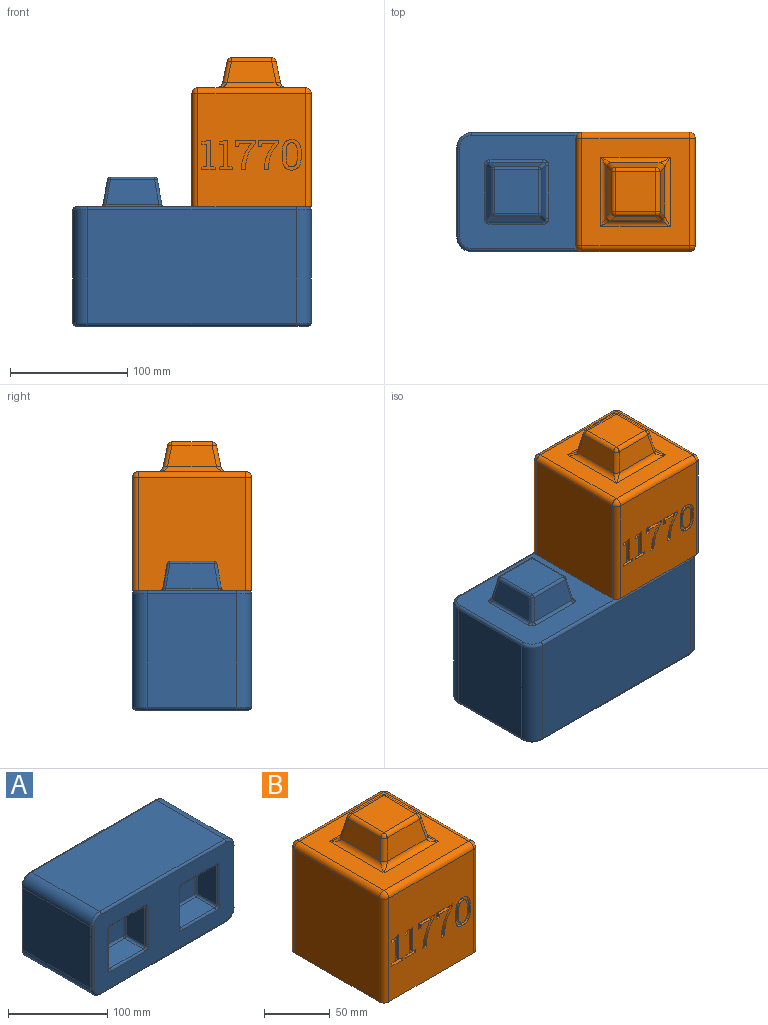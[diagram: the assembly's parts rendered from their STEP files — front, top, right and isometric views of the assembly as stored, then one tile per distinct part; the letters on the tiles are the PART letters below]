
ASSEMBLY  parts=2 mates=1
PART A: 196 faces, bbox 205.4x127.2x103.8 mm
  f0: bspline ~3.55x3.2mm, area 9.5mm2, adj f8,f130,f132,f133
  f1: bspline ~3.55x3.2mm, area 9.5mm2, adj f8,f82,f129,f131
  f2: bspline ~3.55x3.2mm, area 9.5mm2, adj f8,f122,f124,f125
  f3: bspline ~3.55x3.2mm, area 9.5mm2, adj f8,f70,f121,f123
  f4: bspline ~3.55x3.2mm, area 9.5mm2, adj f8,f84,f87,f88
  f5: bspline ~3.55x3.2mm, area 9.5mm2, adj f8,f82,f83,f86
  f6: bspline ~3.55x3.2mm, area 9.5mm2, adj f8,f72,f75,f76
  f7: bspline ~3.55x3.2mm, area 9.5mm2, adj f8,f70,f71,f74
  f8: plane 198.14x96.54mm, normal (0,1,0), area 13012.7mm2, adj f0,f1,f2,f3,f4,f5,f6,f7
  f9: plane 96.52x76.2mm, normal (1,0,0), area 7354.8mm2, adj f29,f31,f40,f94
  f10: plane 177.8x96.52mm, normal (0,0,-1), area 17161.3mm2, adj f29,f30,f33,f37
  f11: plane 96.52x76.2mm, normal (-1,0,0), area 7354.8mm2, adj f30,f34,f38,f95
  f12: plane 198.27x96.67mm, normal (0,-1,0), area 12440.4mm2, adj f36,f37,f38,f39,f40,f46,f47,f49
  f13: plane 45.06x21.2mm, normal (0.98,0.17,0), area 889.6mm2, adj f77,f82,f83,f129
  f14: plane 45.06x21.2mm, normal (0,0.17,-0.98), area 889.6mm2, adj f78,f83,f84,f88
  f15: plane 45.06x21.2mm, normal (-0.98,0.17,0), area 889.6mm2, adj f79,f84,f85,f130
  f16: plane 37.58x37.58mm, normal (0,1,0), area 1412.3mm2, adj f77,f78,f79,f126
  f17: plane 45.06x21.2mm, normal (0.98,0.17,0), area 889.6mm2, adj f65,f70,f71,f121
  f18: plane 45.06x21.2mm, normal (0,0.17,-0.98), area 889.6mm2, adj f66,f71,f72,f76
  f19: plane 45.06x21.2mm, normal (-0.98,0.17,0), area 889.6mm2, adj f67,f72,f73,f122
  f20: plane 37.58x37.58mm, normal (0,1,0), area 1412.3mm2, adj f65,f66,f67,f118
  f21: plane 47.6x22.47mm, normal (-0.98,-0.17,0), area 995.7mm2, adj f45,f50,f52,f108
  f22: plane 47.6x22.47mm, normal (0,-0.17,0.98), area 995.7mm2, adj f43,f44,f49,f50
  f23: plane 47.6x22.47mm, normal (0.98,-0.17,0), area 995.7mm2, adj f41,f43,f46,f103
  f24: plane 39.67x39.67mm, normal (0,-1,0), area 1573.9mm2, adj f41,f44,f45,f104
  f25: plane 47.6x22.47mm, normal (-0.98,-0.17,0), area 995.7mm2, adj f55,f60,f61,f114
  f26: plane 47.6x22.47mm, normal (0,-0.17,0.98), area 995.7mm2, adj f54,f59,f60,f64
  f27: plane 47.6x22.47mm, normal (0.98,-0.17,0), area 995.7mm2, adj f53,f58,f59,f113
  f28: plane 39.67x39.67mm, normal (0,-1,0), area 1573.9mm2, adj f53,f54,f55,f110
  f29: cylinder r=12.7mm len=96.52mm, axis (0,-1,0), area 1925.5mm2, adj f9,f10,f32,f39
  f30: cylinder r=12.7mm len=96.52mm, axis (0,-1,0), area 1925.5mm2, adj f10,f11,f35,f36
  f31: cylinder r=2.54mm len=76.2mm, axis (0,0,-1), area 304mm2, adj f8,f9,f32,f96
  f32: torus R=10.16mm, axis (0,-1,0), area 73.8mm2, adj f8,f29,f31,f33
  f33: cylinder r=2.54mm len=177.8mm, axis (-1,0,0), area 709.4mm2, adj f8,f10,f32,f35
  f34: cylinder r=2.54mm len=76.2mm, axis (0,0,1), area 304mm2, adj f8,f11,f35,f98
  f35: torus R=10.16mm, axis (0,-1,0), area 73.8mm2, adj f8,f30,f33,f34
  f36: torus R=10.16mm, axis (0,-1,0), area 73.8mm2, adj f12,f30,f37,f38
  f37: cylinder r=2.54mm len=177.8mm, axis (1,0,0), area 709.4mm2, adj f10,f12,f36,f39
  f38: cylinder r=2.54mm len=76.2mm, axis (0,0,-1), area 304mm2, adj f11,f12,f36,f99
  f39: torus R=10.16mm, axis (0,-1,0), area 73.8mm2, adj f12,f29,f37,f40
  f40: cylinder r=2.54mm len=76.2mm, axis (0,0,1), area 304mm2, adj f9,f12,f39,f101
  f41: cylinder r=2.54mm len=39.67mm, axis (0,0,-1), area 140.7mm2, adj f23,f24,f42,f102
  f42: sphere r=2.54mm, area 8.4mm2, adj f41,f43,f44
  f43: cylinder r=2.54mm len=22.99mm, axis (0.17,0.97,0.17), area 91.6mm2, adj f22,f23,f42,f47
  f44: cylinder r=2.54mm len=39.67mm, axis (1,0,0), area 140.7mm2, adj f22,f24,f42,f48
  f45: cylinder r=2.54mm len=39.67mm, axis (0,0,1), area 140.7mm2, adj f21,f24,f48,f106
  f46: cylinder r=2.54mm len=47.6mm, axis (0,0,1), area 168.8mm2, adj f12,f23,f47,f105
  f47: bspline ~5x5mm, area 19.1mm2, adj f12,f43,f46,f49
  f48: sphere r=2.54mm, area 7.9mm2, adj f44,f45,f50
  f49: cylinder r=2.54mm len=47.6mm, axis (-1,0,0), area 168.8mm2, adj f12,f22,f47,f51
  f50: cylinder r=2.54mm len=22.99mm, axis (-0.17,0.97,0.17), area 91.6mm2, adj f21,f22,f48,f51
  f51: bspline ~5x5mm, area 19.1mm2, adj f12,f49,f50,f52
  f52: cylinder r=2.54mm len=47.6mm, axis (0,0,-1), area 168.8mm2, adj f12,f21,f51,f109
  f53: cylinder r=2.54mm len=39.67mm, axis (0,0,-1), area 140.7mm2, adj f27,f28,f56,f111
  f54: cylinder r=2.54mm len=39.67mm, axis (1,0,0), area 140.7mm2, adj f26,f28,f56,f57
  f55: cylinder r=2.54mm len=39.67mm, axis (0,0,1), area 140.7mm2, adj f25,f28,f57,f112
  f56: sphere r=2.54mm, area 8.4mm2, adj f53,f54,f59
  f57: sphere r=2.54mm, area 7.9mm2, adj f54,f55,f60
  f58: cylinder r=2.54mm len=47.6mm, axis (0,0,1), area 168.8mm2, adj f12,f27,f62,f115
  f59: cylinder r=2.54mm len=22.99mm, axis (0.17,0.97,0.17), area 91.6mm2, adj f26,f27,f56,f62
  f60: cylinder r=2.54mm len=22.99mm, axis (-0.17,0.97,0.17), area 91.6mm2, adj f25,f26,f57,f63
  f61: cylinder r=2.54mm len=47.6mm, axis (0,0,-1), area 168.8mm2, adj f12,f25,f63,f116
  f62: bspline ~5x5mm, area 19.1mm2, adj f12,f58,f59,f64
  f63: bspline ~5x5mm, area 19.1mm2, adj f12,f60,f61,f64
  f64: cylinder r=2.54mm len=47.6mm, axis (-1,0,0), area 168.8mm2, adj f12,f26,f62,f63
  f65: cylinder r=2.54mm len=37.58mm, axis (0,0,1), area 133.3mm2, adj f17,f20,f68,f119
  f66: cylinder r=2.54mm len=37.58mm, axis (1,0,0), area 133.3mm2, adj f18,f20,f68,f69
  f67: cylinder r=2.54mm len=37.58mm, axis (0,0,-1), area 133.3mm2, adj f19,f20,f69,f120
  f68: sphere r=2.54mm, area 7.9mm2, adj f65,f66,f71
  f69: sphere r=2.54mm, area 8.4mm2, adj f66,f67,f72
  f70: cylinder r=2.54mm len=45.06mm, axis (0,0,-1), area 159.8mm2, adj f3,f7,f8,f17
  f71: cylinder r=2.54mm len=21.72mm, axis (0.17,-0.97,-0.17), area 86.2mm2, adj f7,f17,f18,f68,f74
  f72: cylinder r=2.54mm len=21.72mm, axis (-0.17,-0.97,-0.17), area 86.2mm2, adj f6,f18,f19,f69,f75
  f73: cylinder r=2.54mm len=45.06mm, axis (0,0,1), area 159.8mm2, adj f8,f19,f75,f124
  f74: bspline ~3.55x3.2mm, area 9.5mm2, adj f7,f8,f71,f76
  f75: bspline ~3.55x3.2mm, area 9.5mm2, adj f6,f8,f72,f73
  f76: cylinder r=2.54mm len=45.06mm, axis (-1,0,0), area 159.8mm2, adj f6,f8,f18,f74
  f77: cylinder r=2.54mm len=37.58mm, axis (0,0,1), area 133.3mm2, adj f13,f16,f80,f127
  f78: cylinder r=2.54mm len=37.58mm, axis (1,0,0), area 133.3mm2, adj f14,f16,f80,f81
  f79: cylinder r=2.54mm len=37.58mm, axis (0,0,-1), area 133.3mm2, adj f15,f16,f81,f128
  f80: sphere r=2.54mm, area 7.9mm2, adj f77,f78,f83
  f81: sphere r=2.54mm, area 8.4mm2, adj f78,f79,f84
  f82: cylinder r=2.54mm len=45.06mm, axis (0,0,-1), area 159.8mm2, adj f1,f5,f8,f13
  f83: cylinder r=2.54mm len=21.72mm, axis (0.17,-0.97,-0.17), area 86.2mm2, adj f5,f13,f14,f80,f86
  f84: cylinder r=2.54mm len=21.72mm, axis (-0.17,-0.97,-0.17), area 86.2mm2, adj f4,f14,f15,f81,f87
  f85: cylinder r=2.54mm len=45.06mm, axis (0,0,1), area 159.8mm2, adj f8,f15,f87,f132
  f86: bspline ~3.55x3.2mm, area 9.5mm2, adj f5,f8,f83,f88
  f87: bspline ~3.55x3.2mm, area 9.5mm2, adj f4,f8,f84,f85
  f88: cylinder r=2.54mm len=45.06mm, axis (-1,0,0), area 159.8mm2, adj f4,f8,f14,f86
  f89: plane 177.8x96.52mm, normal (0,0,1), area 17161.3mm2, adj f94,f95,f97,f100
  f90: plane 45.06x21.2mm, normal (0,0.17,0.98), area 889.6mm2, adj f126,f129,f130,f133
  f91: plane 45.06x21.2mm, normal (0,0.17,0.98), area 889.6mm2, adj f118,f121,f122,f125
  f92: plane 47.6x22.47mm, normal (0,-0.17,-0.98), area 995.7mm2, adj f103,f104,f107,f108
  f93: plane 47.6x22.47mm, normal (0,-0.17,-0.98), area 995.7mm2, adj f110,f113,f114,f117
  f94: cylinder r=12.7mm len=96.52mm, axis (0,-1,0), area 1925.5mm2, adj f9,f89,f96,f101
  f95: cylinder r=12.7mm len=96.52mm, axis (0,-1,0), area 1925.5mm2, adj f11,f89,f98,f99
  f96: torus R=10.16mm, axis (0,-1,0), area 73.8mm2, adj f8,f31,f94,f97
  f97: cylinder r=2.54mm len=177.8mm, axis (-1,0,0), area 709.4mm2, adj f8,f89,f96,f98
  f98: torus R=10.16mm, axis (0,-1,0), area 73.8mm2, adj f8,f34,f95,f97
  f99: torus R=10.16mm, axis (0,-1,0), area 73.8mm2, adj f12,f38,f95,f100
  f100: cylinder r=2.54mm len=177.8mm, axis (1,0,0), area 709.4mm2, adj f12,f89,f99,f101
  f101: torus R=10.16mm, axis (0,-1,0), area 73.8mm2, adj f12,f40,f94,f100
  f102: sphere r=2.54mm, area 8.4mm2, adj f41,f103,f104
  f103: cylinder r=2.54mm len=22.99mm, axis (0.17,0.97,-0.17), area 91.6mm2, adj f23,f92,f102,f105
  f104: cylinder r=2.54mm len=39.67mm, axis (1,0,0), area 140.7mm2, adj f24,f92,f102,f106
  f105: bspline ~5x5mm, area 19.1mm2, adj f12,f46,f103,f107
  f106: sphere r=2.54mm, area 7.9mm2, adj f45,f104,f108
  f107: cylinder r=2.54mm len=47.6mm, axis (-1,0,0), area 168.8mm2, adj f12,f92,f105,f109
  f108: cylinder r=2.54mm len=22.99mm, axis (-0.17,0.97,-0.17), area 91.6mm2, adj f21,f92,f106,f109
  f109: bspline ~5x5mm, area 19.1mm2, adj f12,f52,f107,f108
  f110: cylinder r=2.54mm len=39.67mm, axis (1,0,0), area 140.7mm2, adj f28,f93,f111,f112
  f111: sphere r=2.54mm, area 8.4mm2, adj f53,f110,f113
  f112: sphere r=2.54mm, area 7.9mm2, adj f55,f110,f114
  f113: cylinder r=2.54mm len=22.99mm, axis (0.17,0.97,-0.17), area 91.6mm2, adj f27,f93,f111,f115
  f114: cylinder r=2.54mm len=22.99mm, axis (-0.17,0.97,-0.17), area 91.6mm2, adj f25,f93,f112,f116
  f115: bspline ~5x5mm, area 19.1mm2, adj f12,f58,f113,f117
  f116: bspline ~5x5mm, area 19.1mm2, adj f12,f61,f114,f117
  f117: cylinder r=2.54mm len=47.6mm, axis (-1,0,0), area 168.8mm2, adj f12,f93,f115,f116
  f118: cylinder r=2.54mm len=37.58mm, axis (1,0,0), area 133.3mm2, adj f20,f91,f119,f120
  f119: sphere r=2.54mm, area 7.9mm2, adj f65,f118,f121
  f120: sphere r=2.54mm, area 8.4mm2, adj f67,f118,f122
  f121: cylinder r=2.54mm len=21.72mm, axis (0.17,-0.97,0.17), area 86.2mm2, adj f3,f17,f91,f119,f123
  f122: cylinder r=2.54mm len=21.72mm, axis (-0.17,-0.97,0.17), area 86.2mm2, adj f2,f19,f91,f120,f124
  f123: bspline ~3.55x3.2mm, area 9.5mm2, adj f3,f8,f121,f125
  f124: bspline ~3.55x3.2mm, area 9.5mm2, adj f2,f8,f73,f122
  f125: cylinder r=2.54mm len=45.06mm, axis (-1,0,0), area 159.8mm2, adj f2,f8,f91,f123
  f126: cylinder r=2.54mm len=37.58mm, axis (1,0,0), area 133.3mm2, adj f16,f90,f127,f128
  f127: sphere r=2.54mm, area 7.9mm2, adj f77,f126,f129
  f128: sphere r=2.54mm, area 8.4mm2, adj f79,f126,f130
  f129: cylinder r=2.54mm len=21.72mm, axis (0.17,-0.97,0.17), area 86.2mm2, adj f1,f13,f90,f127,f131
  f130: cylinder r=2.54mm len=21.72mm, axis (-0.17,-0.97,0.17), area 86.2mm2, adj f0,f15,f90,f128,f132
  f131: bspline ~3.55x3.2mm, area 9.5mm2, adj f1,f8,f129,f133
  f132: bspline ~3.55x3.2mm, area 9.5mm2, adj f0,f8,f85,f130
  f133: cylinder r=2.54mm len=45.06mm, axis (-1,0,0), area 159.8mm2, adj f0,f8,f90,f131
  f134: sphere r=5.08mm, area 31.7mm2, adj f135,f145,f194
  f135: cylinder r=5.08mm len=39.67mm, axis (1,0,0), area 281.4mm2, adj f134,f136,f144,f193
  f136: sphere r=5.08mm, area 31.7mm2, adj f135,f143,f192
  f137: sphere r=5.08mm, area 31.7mm2, adj f138,f142,f189
  f138: cylinder r=5.08mm len=39.67mm, axis (1,0,0), area 281.4mm2, adj f137,f139,f141,f188
  f139: sphere r=5.08mm, area 31.7mm2, adj f138,f140,f187
  f140: cylinder r=5.08mm len=23.17mm, axis (0.17,0.97,-0.17), area 183.1mm2, adj f139,f141,f185,f186
  f141: plane 47.6x22.47mm, normal (0,0.17,0.98), area 995.7mm2, adj f138,f140,f142,f185
  f142: cylinder r=5.08mm len=23.17mm, axis (-0.17,0.97,-0.17), area 183.1mm2, adj f137,f141,f185,f190
  f143: cylinder r=5.08mm len=23.17mm, axis (0.17,0.97,-0.17), area 183.1mm2, adj f136,f144,f185,f191
  f144: plane 47.6x22.47mm, normal (0,0.17,0.98), area 995.7mm2, adj f135,f143,f145,f185
  f145: cylinder r=5.08mm len=23.17mm, axis (-0.17,0.97,-0.17), area 183.1mm2, adj f134,f144,f185,f195
  f146: plane 45.06x21.2mm, normal (0,-0.17,-0.98), area 889.6mm2, adj f151,f180,f181,f182
  f147: plane 45.06x21.2mm, normal (0,-0.17,-0.98), area 889.6mm2, adj f150,f175,f176,f177
  f148: cylinder r=10.16mm len=96.52mm, axis (0,-1,0), area 1540.4mm2, adj f149,f173,f184,f185
  f149: plane 177.8x96.52mm, normal (0,0,-1), area 17161.3mm2, adj f148,f152,f173,f185
  f150: cylinder r=5.08mm len=55.06mm, axis (-1,0,0), area 347.9mm2, adj f147,f173,f174,f178
  f151: cylinder r=5.08mm len=55.06mm, axis (-1,0,0), area 347.9mm2, adj f146,f173,f179,f183
  f152: cylinder r=10.16mm len=96.52mm, axis (0,-1,0), area 1540.4mm2, adj f149,f172,f173,f185
  f153: sphere r=5.08mm, area 31.7mm2, adj f154,f159,f194
  f154: cylinder r=5.08mm len=39.67mm, axis (1,0,0), area 281.4mm2, adj f153,f155,f160,f193
  f155: sphere r=5.08mm, area 31.7mm2, adj f154,f161,f192
  f156: sphere r=5.08mm, area 31.7mm2, adj f157,f162,f189
  f157: cylinder r=5.08mm len=39.67mm, axis (1,0,0), area 281.4mm2, adj f156,f158,f163,f188
  f158: sphere r=5.08mm, area 31.7mm2, adj f157,f164,f187
  f159: cylinder r=5.08mm len=23.17mm, axis (-0.17,0.97,0.17), area 183.1mm2, adj f153,f160,f185,f195
  f160: plane 47.6x22.47mm, normal (0,0.17,-0.98), area 995.7mm2, adj f154,f159,f161,f185
  f161: cylinder r=5.08mm len=23.17mm, axis (0.17,0.97,0.17), area 183.1mm2, adj f155,f160,f185,f191
  f162: cylinder r=5.08mm len=23.17mm, axis (-0.17,0.97,0.17), area 183.1mm2, adj f156,f163,f185,f190
  f163: plane 47.6x22.47mm, normal (0,0.17,-0.98), area 995.7mm2, adj f157,f162,f164,f185
  f164: cylinder r=5.08mm len=23.17mm, axis (0.17,0.97,0.17), area 183.1mm2, adj f158,f163,f185,f186
  f165: plane 45.06x21.2mm, normal (0,-0.17,0.98), area 889.6mm2, adj f167,f180,f181,f182
  f166: plane 45.06x21.2mm, normal (0,-0.17,0.98), area 889.6mm2, adj f168,f175,f176,f177
  f167: cylinder r=5.08mm len=55.06mm, axis (-1,0,0), area 347.9mm2, adj f165,f173,f179,f183
  f168: cylinder r=5.08mm len=55.06mm, axis (-1,0,0), area 347.9mm2, adj f166,f173,f174,f178
  f169: plane 177.8x96.52mm, normal (0,0,1), area 17161.3mm2, adj f170,f171,f173,f185
  f170: cylinder r=10.16mm len=96.52mm, axis (0,-1,0), area 1540.4mm2, adj f169,f173,f184,f185
  f171: cylinder r=10.16mm len=96.52mm, axis (0,-1,0), area 1540.4mm2, adj f169,f172,f173,f185
  f172: plane 96.52x76.2mm, normal (-1,0,0), area 7354.8mm2, adj f152,f171,f173,f185
  f173: plane 198.12x96.52mm, normal (0,-1,0), area 12970.1mm2, adj f148,f149,f150,f151,f152,f167,f168,f169
  f174: cylinder r=5.08mm len=55.06mm, axis (0,0,-1), area 347.9mm2, adj f150,f168,f173,f175
  f175: plane 45.06x21.2mm, normal (-0.98,-0.17,0), area 889.6mm2, adj f147,f166,f174,f176
  f176: plane 37.58x37.58mm, normal (0,-1,0), area 1412.3mm2, adj f147,f166,f175,f177
  f177: plane 45.06x21.2mm, normal (0.98,-0.17,0), area 889.6mm2, adj f147,f166,f176,f178
  f178: cylinder r=5.08mm len=55.06mm, axis (0,0,1), area 347.9mm2, adj f150,f168,f173,f177
  f179: cylinder r=5.08mm len=55.06mm, axis (0,0,-1), area 347.9mm2, adj f151,f167,f173,f180
  f180: plane 45.06x21.2mm, normal (-0.98,-0.17,0), area 889.6mm2, adj f146,f165,f179,f181
  f181: plane 37.58x37.58mm, normal (0,-1,0), area 1412.3mm2, adj f146,f165,f180,f182
  f182: plane 45.06x21.2mm, normal (0.98,-0.17,0), area 889.6mm2, adj f146,f165,f181,f183
  f183: cylinder r=5.08mm len=55.06mm, axis (0,0,1), area 347.9mm2, adj f151,f167,f173,f182
  f184: plane 96.52x76.2mm, normal (1,0,0), area 7354.8mm2, adj f148,f170,f173,f185
  f185: plane 198.12x96.52mm, normal (0,1,0), area 12440.4mm2, adj f140,f141,f142,f143,f144,f145,f148,f149
  f186: plane 47.6x22.47mm, normal (-0.98,0.17,0), area 995.7mm2, adj f140,f164,f185,f187
  f187: cylinder r=5.08mm len=39.67mm, axis (0,0,-1), area 281.4mm2, adj f139,f158,f186,f188
  f188: plane 39.67x39.67mm, normal (0,1,0), area 1573.9mm2, adj f138,f157,f187,f189
  f189: cylinder r=5.08mm len=39.67mm, axis (0,0,1), area 281.4mm2, adj f137,f156,f188,f190
  f190: plane 47.6x22.47mm, normal (0.98,0.17,0), area 995.7mm2, adj f142,f162,f185,f189
  f191: plane 47.6x22.47mm, normal (-0.98,0.17,0), area 995.7mm2, adj f143,f161,f185,f192
  f192: cylinder r=5.08mm len=39.67mm, axis (0,0,-1), area 281.4mm2, adj f136,f155,f191,f193
  f193: plane 39.67x39.67mm, normal (0,1,0), area 1573.9mm2, adj f135,f154,f192,f194
  f194: cylinder r=5.08mm len=39.67mm, axis (0,0,1), area 281.4mm2, adj f134,f153,f193,f195
  f195: plane 47.6x22.47mm, normal (0.98,0.17,0), area 995.7mm2, adj f145,f159,f185,f194
PART B: 147 faces, bbox 101.6x101.6x127 mm
  f0: plane 96.52x91.44mm, normal (0,-1,0), area 7979.3mm2, adj f1,f18,f45,f46,f47,f48,f49,f50
  f1: plane 101.6x101.6mm, normal (0,0,-1), area 6406.6mm2, adj f0,f3,f4,f5,f19,f20,f21,f22
  f2: plane 91.44x91.44mm, normal (0,0,1), area 4865mm2, adj f11,f12,f13,f14,f15,f16,f17,f18
  f3: plane 96.52x91.44mm, normal (0,1,0), area 6128.8mm2, adj f1,f15,f108,f109,f110,f111,f112,f113
  f4: plane 96.52x91.44mm, normal (-1,0,0), area 8825.8mm2, adj f1,f16,f123,f127
  f5: plane 96.52x91.44mm, normal (1,0,0), area 8825.8mm2, adj f1,f17,f125,f129
  f6: plane 34.39x34.39mm, normal (0,0,1), area 1182.9mm2, adj f137,f138,f142,f143
  f7: plane 41.69x18.25mm, normal (0,-0.98,0.2), area 708.2mm2, adj f14,f139,f143,f145
  f8: plane 41.69x18.25mm, normal (-0.98,0,0.2), area 708.2mm2, adj f12,f136,f142,f145
  f9: plane 41.69x18.25mm, normal (0.98,0,0.2), area 708.2mm2, adj f13,f132,f138,f139
  f10: plane 41.69x18.25mm, normal (0,0.98,0.2), area 708.2mm2, adj f11,f132,f136,f137
  f11: cylinder r=5.08mm len=59.13mm, axis (1,0,0), area 339.9mm2, adj f2,f10,f131,f133
  f12: cylinder r=5.08mm len=59.13mm, axis (0,1,0), area 339.9mm2, adj f2,f8,f133,f146
  f13: cylinder r=5.08mm len=59.13mm, axis (0,-1,0), area 339.9mm2, adj f2,f9,f131,f135
  f14: cylinder r=5.08mm len=59.13mm, axis (-1,0,0), area 339.9mm2, adj f2,f7,f135,f146
  f15: cylinder r=5.08mm len=91.44mm, axis (1,0,0), area 729.7mm2, adj f2,f3,f124,f126
  f16: cylinder r=5.08mm len=91.44mm, axis (0,1,0), area 729.7mm2, adj f2,f4,f124,f128
  f17: cylinder r=5.08mm len=91.44mm, axis (0,-1,0), area 729.7mm2, adj f2,f5,f126,f130
  f18: cylinder r=5.08mm len=91.44mm, axis (-1,0,0), area 729.7mm2, adj f0,f2,f128,f130
  f19: plane 90.17x38.1mm, normal (0,-1,0), area 3435.5mm2, adj f1,f24,f27,f28
  f20: plane 90.17x38.1mm, normal (-1,0,0), area 3435.5mm2, adj f1,f24,f25,f31
  f21: plane 90.17x38.1mm, normal (0,1,0), area 3435.5mm2, adj f1,f25,f26,f35
  f22: plane 90.17x38.1mm, normal (1,0,0), area 3435.5mm2, adj f1,f26,f27,f32
  f23: plane 53.34x53.34mm, normal (0,0,-1), area 2795.3mm2, adj f28,f29,f30,f31,f32,f33,f34,f35
  f24: cylinder r=12.7mm len=90.17mm, axis (0,0,-1), area 1798.8mm2, adj f1,f19,f20,f29
  f25: cylinder r=12.7mm len=90.17mm, axis (0,0,1), area 1798.8mm2, adj f1,f20,f21,f33
  f26: cylinder r=12.7mm len=90.17mm, axis (0,0,-1), area 1798.8mm2, adj f1,f21,f22,f34
  f27: cylinder r=12.7mm len=90.17mm, axis (0,0,1), area 1798.8mm2, adj f1,f19,f22,f30
  f28: plane 38.1x5.08mm, normal (0,-0.71,-0.71), area 273.7mm2, adj f19,f23,f29,f30
  f29: cone r=7.62mm half-angle=45deg, axis (0,0,-1), area 114.7mm2, adj f23,f24,f28,f31
  f30: cone r=7.62mm half-angle=45deg, axis (0,0,-1), area 114.7mm2, adj f23,f27,f28,f32
  f31: plane 38.1x5.08mm, normal (-0.71,0,-0.71), area 273.7mm2, adj f20,f23,f29,f33
  f32: plane 38.1x5.08mm, normal (0.71,0,-0.71), area 273.7mm2, adj f22,f23,f30,f34
  f33: cone r=7.62mm half-angle=45deg, axis (0,0,-1), area 114.7mm2, adj f23,f25,f31,f35
  f34: cone r=7.62mm half-angle=45deg, axis (0,0,-1), area 114.7mm2, adj f23,f26,f32,f35
  f35: plane 38.1x5.08mm, normal (0,0.71,-0.71), area 273.7mm2, adj f21,f23,f33,f34
  f36: extruded ~4.94x2.54mm, area 13.1mm2, adj f37,f55,f56,f107
  f37: plane 7.42x2.54mm, normal (1,0,0), area 18.8mm2, adj f36,f38,f56,f107
  f38: extruded ~4.96x2.54mm, area 13.1mm2, adj f37,f39,f56,f107
  f39: extruded ~3.45x2.54mm, area 10.1mm2, adj f38,f40,f56,f107
  f40: extruded ~3.44x2.54mm, area 10.1mm2, adj f39,f41,f56,f107
  f41: extruded ~4.95x2.54mm, area 13.1mm2, adj f40,f42,f56,f107
  f42: plane 7.42x2.54mm, normal (-1,0,0), area 18.8mm2, adj f41,f43,f56,f107
  f43: extruded ~4.94x2.54mm, area 13.1mm2, adj f42,f44,f56,f107
  f44: extruded ~3.42x2.54mm, area 10.1mm2, adj f43,f55,f56,f107
  f45: extruded ~7.42x2.54mm, area 20mm2, adj f0,f46,f54,f56
  f46: plane 6x2.54mm, normal (-1,0,0), area 15.2mm2, adj f0,f45,f47,f56
  f47: extruded ~7.42x2.54mm, area 20mm2, adj f0,f46,f48,f56
  f48: extruded ~5.9x2.6mm, area 17mm2, adj f0,f47,f49,f56
  f49: extruded ~5.87x2.6mm, area 16.9mm2, adj f0,f48,f50,f56
  f50: extruded ~7.42x2.54mm, area 20mm2, adj f0,f49,f51,f56
  f51: plane 6x2.54mm, normal (1,0,0), area 15.2mm2, adj f0,f50,f52,f56
  f52: extruded ~7.41x2.54mm, area 20mm2, adj f0,f51,f53,f56
  f53: extruded ~5.89x2.59mm, area 16.9mm2, adj f0,f52,f54,f56
  f54: extruded ~5.89x2.58mm, area 16.9mm2, adj f0,f45,f53,f56
  f55: extruded ~3.46x2.54mm, area 10.2mm2, adj f36,f44,f56,f107
  f56: plane 26.02x16.1mm, normal (0,-1,0), area 190.5mm2, adj f36,f37,f38,f39,f40,f41,f42,f43
  f57: extruded ~9.67x6.19mm, area 29.3mm2, adj f0,f58,f69,f70
  f58: plane 2.69x2.54mm, normal (-1,0,0), area 6.8mm2, adj f0,f57,f59,f70
  f59: plane 17.09x2.54mm, normal (0,0,-1), area 43.4mm2, adj f0,f58,f60,f70
  f60: plane 5.59x2.54mm, normal (1,0,0), area 14.2mm2, adj f0,f59,f61,f70
  f61: plane 2.92x2.54mm, normal (0,0,1), area 7.4mm2, adj f0,f60,f62,f70
  f62: plane 2.9x2.54mm, normal (-1,0,0.09), area 7.4mm2, adj f0,f61,f63,f70
  f63: plane 10.56x2.54mm, normal (0,0,1), area 26.8mm2, adj f0,f62,f64,f70
  f64: extruded ~9.19x5.75mm, area 27.6mm2, adj f0,f63,f65,f70
  f65: extruded ~10.68x2.83mm, area 28.2mm2, adj f0,f64,f66,f70
  f66: plane 2.73x2.54mm, normal (0.99,0,-0.1), area 7mm2, adj f0,f65,f67,f70
  f67: plane 3.42x2.54mm, normal (0,0,1), area 8.7mm2, adj f0,f66,f68,f70
  f68: plane 2.73x2.54mm, normal (-0.99,0,0.1), area 7mm2, adj f0,f67,f69,f70
  f69: extruded ~10.2x2.54mm, area 26.6mm2, adj f0,f57,f68,f70
  f70: plane 25.28x17.09mm, normal (0,-1,0), area 128.6mm2, adj f57,f58,f59,f60,f61,f62,f63,f64
  f71: extruded ~9.67x6.19mm, area 29.3mm2, adj f0,f72,f83,f84
  f72: plane 2.69x2.54mm, normal (-1,0,0), area 6.8mm2, adj f0,f71,f73,f84
  f73: plane 17.09x2.54mm, normal (0,0,-1), area 43.4mm2, adj f0,f72,f74,f84
  f74: plane 5.59x2.54mm, normal (1,0,0), area 14.2mm2, adj f0,f73,f75,f84
  f75: plane 2.92x2.54mm, normal (0,0,1), area 7.4mm2, adj f0,f74,f76,f84
  f76: plane 2.9x2.54mm, normal (-1,0,0.09), area 7.4mm2, adj f0,f75,f77,f84
  f77: plane 10.56x2.54mm, normal (0,0,1), area 26.8mm2, adj f0,f76,f78,f84
  f78: extruded ~9.19x5.75mm, area 27.6mm2, adj f0,f77,f79,f84
  f79: extruded ~10.68x2.83mm, area 28.2mm2, adj f0,f78,f80,f84
  f80: plane 2.73x2.54mm, normal (0.99,0,-0.1), area 7mm2, adj f0,f79,f81,f84
  f81: plane 3.42x2.54mm, normal (0,0,1), area 8.7mm2, adj f0,f80,f82,f84
  f82: plane 2.73x2.54mm, normal (-0.99,0,0.1), area 7mm2, adj f0,f81,f83,f84
  f83: extruded ~10.2x2.54mm, area 26.6mm2, adj f0,f71,f82,f84
  f84: plane 25.28x17.09mm, normal (0,-1,0), area 128.6mm2, adj f71,f72,f73,f74,f75,f76,f77,f78
  f85: plane 3.91x2.54mm, normal (0.12,0,-0.99), area 10mm2, adj f0,f86,f94,f95
  f86: plane 2.54x2.19mm, normal (1,0,0), area 5.6mm2, adj f0,f85,f87,f95
  f87: plane 11.22x2.54mm, normal (0,0,1), area 28.5mm2, adj f0,f86,f88,f95
  f88: plane 2.54x2.19mm, normal (-1,0,0), area 5.6mm2, adj f0,f87,f89,f95
  f89: plane 3.89x2.54mm, normal (-0.12,0,-0.99), area 10mm2, adj f0,f88,f90,f95
  f90: plane 22.61x2.54mm, normal (-1,0,0), area 57.4mm2, adj f0,f89,f91,f95
  f91: plane 7.4x2.54mm, normal (0.21,0,-0.98), area 19.2mm2, adj f0,f90,f92,f95
  f92: plane 2.54x2.14mm, normal (1,0,0), area 5.4mm2, adj f0,f91,f93,f95
  f93: plane 3.97x2.54mm, normal (-0.02,0,1), area 10.1mm2, adj f0,f92,f94,f95
  f94: plane 18.95x2.54mm, normal (1,0,0), area 48.1mm2, adj f0,f85,f93,f95
  f95: plane 25.28x11.29mm, normal (0,-1,0), area 114.3mm2, adj f85,f86,f87,f88,f89,f90,f91,f92
  f96: plane 3.91x2.54mm, normal (0.12,0,-0.99), area 10mm2, adj f0,f97,f105,f106
  f97: plane 2.54x2.19mm, normal (1,0,0), area 5.6mm2, adj f0,f96,f98,f106
  f98: plane 11.22x2.54mm, normal (0,0,1), area 28.5mm2, adj f0,f97,f99,f106
  f99: plane 2.54x2.19mm, normal (-1,0,0), area 5.6mm2, adj f0,f98,f100,f106
  f100: plane 3.89x2.54mm, normal (-0.12,0,-0.99), area 10mm2, adj f0,f99,f101,f106
  f101: plane 22.61x2.54mm, normal (-1,0,0), area 57.4mm2, adj f0,f100,f102,f106
  f102: plane 7.4x2.54mm, normal (0.21,0,-0.98), area 19.2mm2, adj f0,f101,f103,f106
  f103: plane 2.54x2.14mm, normal (1,0,0), area 5.4mm2, adj f0,f102,f104,f106
  f104: plane 3.97x2.54mm, normal (-0.02,0,1), area 10.1mm2, adj f0,f103,f105,f106
  f105: plane 18.95x2.54mm, normal (1,0,0), area 48.1mm2, adj f0,f96,f104,f106
  f106: plane 25.28x11.29mm, normal (0,-1,0), area 114.3mm2, adj f96,f97,f98,f99,f100,f101,f102,f103
  f107: plane 20.64x9.25mm, normal (0,-1,0), area 170.1mm2, adj f36,f37,f38,f39,f40,f41,f42,f43
  f108: plane 31.83x5.11mm, normal (-0.16,0,0.99), area 81.9mm2, adj f3,f109,f119,f120
  f109: cylinder r=7.51mm len=3.37mm, axis (0,1,0), area 8.8mm2, adj f3,f108,f110,f120
  f110: plane 32.43x18.75mm, normal (-0.5,0,-0.87), area 95.2mm2, adj f3,f109,f111,f120
  f111: plane 2.54x1.52mm, normal (-0.87,0,0.5), area 4.5mm2, adj f3,f110,f112,f120
  f112: plane 32.43x18.75mm, normal (0.5,0,0.87), area 95.2mm2, adj f3,f111,f113,f120
  f113: cylinder r=7.51mm len=2.54mm, axis (0,1,0), area 8.5mm2, adj f3,f112,f114,f120
  f114: plane 30.28x9.5mm, normal (-0.95,0,-0.3), area 80.6mm2, adj f3,f113,f115,f120
  f115: plane 2.54x1.35mm, normal (0,0,1), area 3.4mm2, adj f3,f114,f116,f120
  f116: plane 29.78x9.34mm, normal (0.95,0,0.3), area 79.3mm2, adj f3,f115,f117,f120
  f117: cylinder r=7.51mm len=15.03mm, axis (0,1,0), area 91.8mm2, adj f3,f116,f118,f120
  f118: plane 31.98x5.13mm, normal (0.16,0,-0.99), area 82.3mm2, adj f3,f117,f119,f120
  f119: plane 2.54x1.2mm, normal (-1,0,0), area 3.1mm2, adj f3,f108,f118,f120
  f120: plane 46.84x44.44mm, normal (0,1,0), area 322.1mm2, adj f108,f109,f110,f111,f112,f113,f114,f115
  f121: extruded ~92.01x81.71mm, area 845mm2, adj f3,f122
  f122: plane 92.76x82.49mm, normal (0,1,0), area 2333.9mm2, adj f121
  f123: cylinder r=5.08mm len=96.52mm, axis (0,0,1), area 770.2mm2, adj f1,f3,f4,f124
  f124: sphere r=5.08mm, area 40.5mm2, adj f15,f16,f123
  f125: cylinder r=5.08mm len=96.52mm, axis (0,0,-1), area 770.2mm2, adj f1,f3,f5,f126
  f126: sphere r=5.08mm, area 40.5mm2, adj f15,f17,f125
  f127: cylinder r=5.08mm len=96.52mm, axis (0,0,-1), area 770.2mm2, adj f0,f1,f4,f128
  f128: sphere r=5.08mm, area 40.5mm2, adj f16,f18,f127
  f129: cylinder r=5.08mm len=96.52mm, axis (0,0,1), area 770.2mm2, adj f0,f1,f5,f130
  f130: sphere r=5.08mm, area 40.5mm2, adj f17,f18,f129
  f131: bspline ~8.78x8.78mm, area 30.9mm2, adj f11,f13,f132
  f132: cylinder r=3.81mm len=18.54mm, axis (0.19,0.19,-0.96), area 110.7mm2, adj f9,f10,f131,f134
  f133: bspline ~8.78x8.78mm, area 30.9mm2, adj f11,f12,f136
  f134: sphere r=3.81mm, area 17.2mm2, adj f132,f137,f138
  f135: bspline ~8.78x8.78mm, area 30.9mm2, adj f13,f14,f139
  f136: cylinder r=3.81mm len=18.54mm, axis (-0.19,0.19,-0.96), area 110.7mm2, adj f8,f10,f133,f140
  f137: cylinder r=3.81mm len=34.39mm, axis (1,0,0), area 180mm2, adj f6,f10,f134,f140
  f138: cylinder r=3.81mm len=34.39mm, axis (0,-1,0), area 180mm2, adj f6,f9,f134,f141
  f139: cylinder r=3.81mm len=18.54mm, axis (-0.19,0.19,0.96), area 110.7mm2, adj f7,f9,f135,f141
  f140: sphere r=3.81mm, area 17.2mm2, adj f136,f137,f142
  f141: sphere r=3.81mm, area 17.2mm2, adj f138,f139,f143
  f142: cylinder r=3.81mm len=34.39mm, axis (0,-1,0), area 180mm2, adj f6,f8,f140,f144
  f143: cylinder r=3.81mm len=34.39mm, axis (1,0,0), area 180mm2, adj f6,f7,f141,f144
  f144: sphere r=3.81mm, area 17.2mm2, adj f142,f143,f145
  f145: cylinder r=3.81mm len=18.54mm, axis (0.19,0.19,0.96), area 110.7mm2, adj f7,f8,f144,f146
  f146: bspline ~8.78x8.78mm, area 30.9mm2, adj f12,f14,f145
PLACE A rot(axis=(1,0,0),90deg) t=(-110.91,-47.54,43.81)mm
PLACE B t=(-60.11,-47.54,145.41)mm
MATE fastened B.f1 <-> A.f8  axis (0,0,-1) through (-60.11,-47.54,145.41)mm
